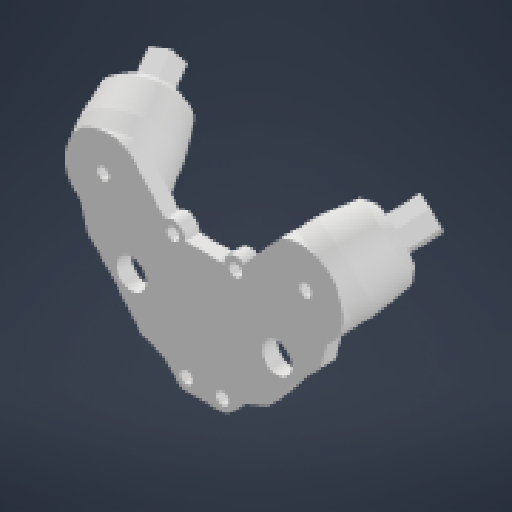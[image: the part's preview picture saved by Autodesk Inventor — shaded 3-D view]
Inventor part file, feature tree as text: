
AUTODESK INVENTOR PART (.ipt)
format: ipt  version: 2024 (Build 280153000, 153)  size: 263,680 bytes
history: native  units: in
note: dims shown in document units (in); Inventor stores cm internally (conversion verified against a paired STEP export)
features: extrude x8, sketch x8, reference x6, other x4, chamfer x3, projected_geometry x3, plane x1
ambient origin geometry x8: Origin, YZ Plane, XZ Plane, XY Plane, X Axis, Y Axis, Z Axis, Center Point
bodies: Solid1 (feature_tree)
feature tree (33):
  extrude  "Extrusion1"  Depth=0.3878in TaperAngle=0.0deg
  plane  "Work Plane1"
  extrude  "Extrusion2"  Depth=0.7087in TaperAngle=0.0deg
  extrude  "Extrusion3"  Depth=0.1969in TaperAngle=45.0deg
  extrude  "Extrusion4"  Depth=0.3937in
  chamfer  "Chamfer1"  Distance=0.1969in
  extrude  "Extrusion5"  Depth=0.1969in TaperAngle=0.0deg
  extrude  "Extrusion6"  Depth=0.1969in TaperAngle=0.0deg
  extrude  "Extrusion7"  Depth=0.0787in
  chamfer  "Chamfer2"  Distance=0.1142in
  chamfer  "Chamfer3"  Distance=0.1654in
  extrude  "Extrusion8"  Depth=0.2756in TaperAngle=0.0deg
  sketch  "Sketch1"  dims[d0=0.1969in d1=0.3878in d2=0.0in]
  reference  "Reference1"
  sketch  "Sketch2"  dims[d3=0.4665in d4=0.0in d5=0.7087in d6=0.0in]
  reference  "Reference2"
  sketch  "Sketch3"  dims[d8=0.1969in d9=0.0in d10=0.1142in d11=0.125in d12=45.0deg]
  reference  "Reference3"
  reference  "Reference4"
  sketch  "Sketch4"  dims[d15=0.3937in d16=0.1654in]
  reference  "Reference5"
  reference  "Reference6"
  sketch  "Sketch5"  dims[d17=0.0787in]
  projected_geometry  "Projected Loop1"
  sketch  "Sketch6"  dims[d18=0.2362in]
  sketch  "Sketch7"  dims[d19=0.1654in]
  projected_geometry  "Projected Loop2"
  sketch  "Sketch8"  dims[d20=0.0787in d21=0.1969in d22=0.0in d23=0.1969in d24=0.0in d25=0.1969in d26=0.0in d27=0.5517in d28=0.125in d29=0.055in d30=0.1142in d31=0.125in d32=0.055in d34=0.1654in d35=0.2756in d36=0.0in d40=0.3937in d41=0.3937in d42=0.0787in d43=0.0in]
  projected_geometry  "Projected Loop3"
  other  "<userpath>\Desktop\Camera_Mount.iam"
  other  "Camera_Mount.iam"
  other  "Universal_Joint:2"
  other  "Universal_Joint_Connector:2"
